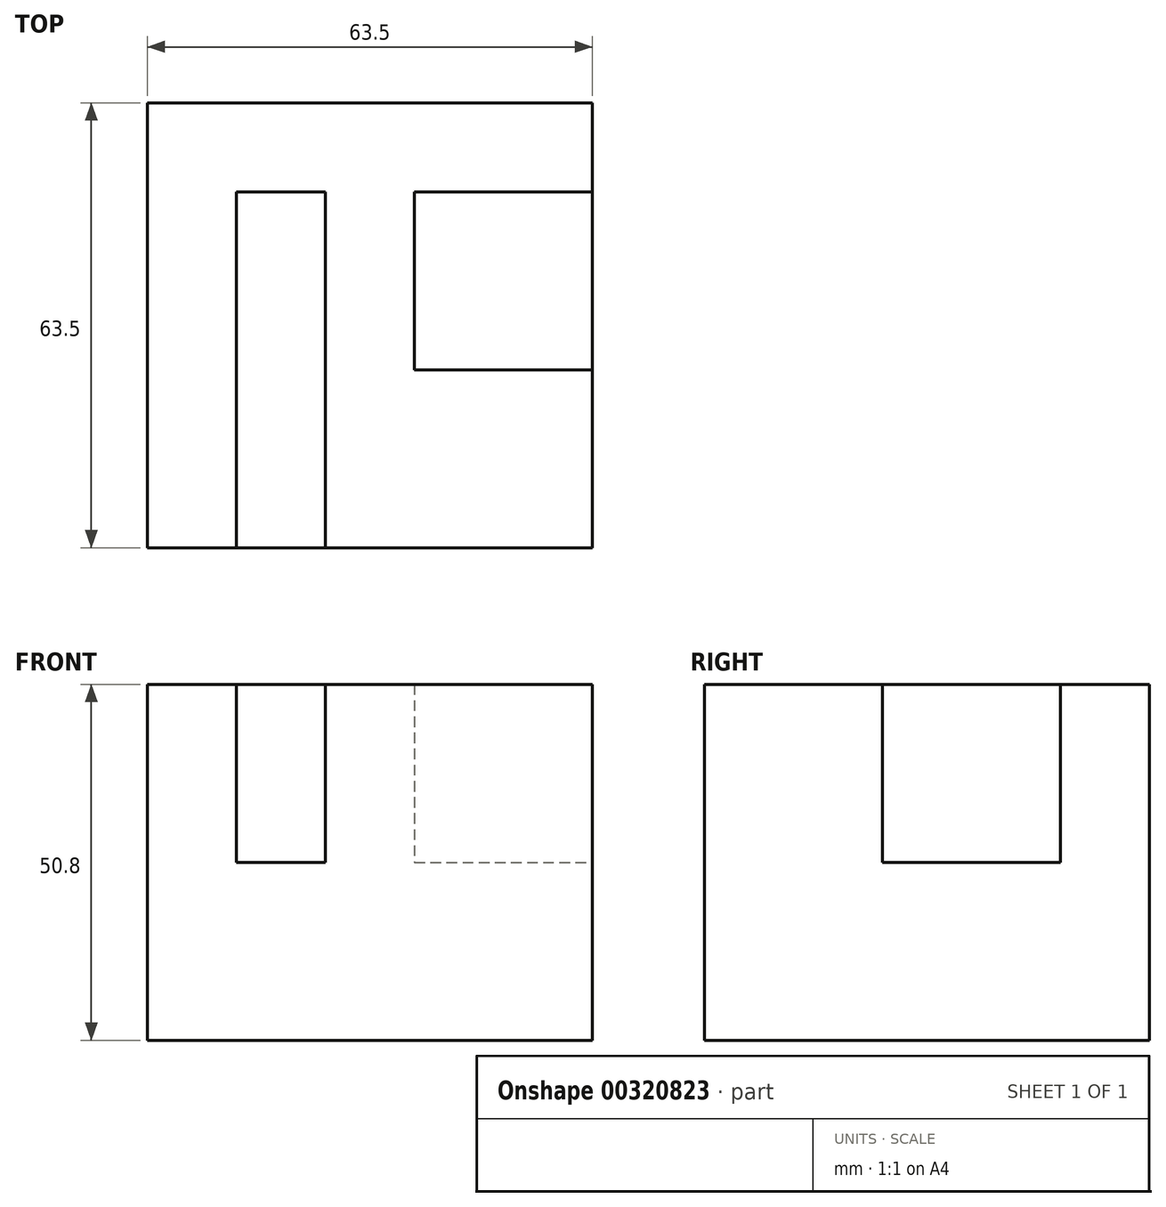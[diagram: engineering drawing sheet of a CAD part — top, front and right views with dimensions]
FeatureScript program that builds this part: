
annotation { "Feature Type Name" : "Feature", "Feature Type Description" : "" }
export const myFeature = defineFeature(function(context is Context, id is Id, definition is map)
    precondition{}
    {
        {
            var Q0;
            Q0=qCreatedBy(makeId("Front.planeOp"),FACE);
            var sketch = newSketch(context, id + "F0", { "sketchPlane" : qUnion([Q0])});
            skLineSegment(sketch, "E0", {"start": v(-39.9, -57.03) * mm, "end": v(23.6, -57.03) * mm});
            skLineSegment(sketch, "E1", {"start": v(23.6, -57.03) * mm, "end": v(23.6, -6.23) * mm});
            skLineSegment(sketch, "E2", {"start": v(23.6, -6.23) * mm, "end": v(-39.9, -6.23) * mm});
            skLineSegment(sketch, "E3", {"start": v(-39.9, -6.23) * mm, "end": v(-39.9, -57.03) * mm});
            skSolve(sketch);
        }
        {
            var Q0;
            Q0=makeQuery(id+"F0.imprint","IMPRINT",FACE,{"disambiguationData":[TD([[makeQuery(id+"F0.imprint","IMPRINT",EDGE,{"derivedFrom":sQuery(id+"F0.wireOp",EDGE,"E0")}),1.0]])]});
            extrude(context, id + "F1", {"entities" : qUnion([Q0]), "oppositeDirection" : true, "depth" : 63.5 * mm});
        }
        {
            var Q0;
            Q0=makeQuery(id+"F1.opExtrude","CAP_FACE",FACE,{"disambiguationData":[OSD([sQuery(id+"F0.wireOp",EDGE,"E0"),sQuery(id+"F0.wireOp",EDGE,"E1"),sQuery(id+"F0.wireOp",EDGE,"E2"),sQuery(id+"F0.wireOp",EDGE,"E3")])],"isStart":true});
            var sketch = newSketch(context, id + "F2", { "sketchPlane" : qUnion([Q0])});
            skLineSegment(sketch, "E4", {"start": v(-39.9, -6.23) * mm, "end": v(-27.2, -6.23) * mm});
            skLineSegment(sketch, "E5", {"start": v(-27.2, -6.23) * mm, "end": v(-14.5, -6.23) * mm});
            skLineSegment(sketch, "E6", {"start": v(-14.5, -6.23) * mm, "end": v(-14.5, -31.63) * mm});
            skLineSegment(sketch, "E7", {"start": v(-14.5, -31.63) * mm, "end": v(-27.2, -31.63) * mm});
            skLineSegment(sketch, "E8", {"start": v(-27.2, -31.63) * mm, "end": v(-27.2, -6.23) * mm});
            skLineSegment(sketch, "E9", {"start": v(-14.5, -6.23) * mm, "end": v(-27.2, -6.23) * mm});
            skSolve(sketch);
        }
        {
            var Q0;
            Q0=makeQuery(id+"F2.imprint","IMPRINT",FACE,{"disambiguationData":[TD([[makeQuery(id+"F2.imprint","IMPRINT",EDGE,{"derivedFrom":sQuery(id+"F2.wireOp",EDGE,"E6")}),-1.0]])]});
            extrude(context, id + "F3", {"entities" : qUnion([Q0]), "operationType" : NewBodyOperationType.REMOVE, "oppositeDirection" : true, "depth" : 50.8 * mm});
        }
        {
            var Q0;
            Q0=makeQuery(id+"F1.opExtrude","SWEPT_FACE",FACE,{"disambiguationData":[OSD([sQuery(id+"F0.wireOp",EDGE,"E1")])]});
            var sketch = newSketch(context, id + "F4", { "sketchPlane" : qUnion([Q0])});
            skLineSegment(sketch, "E10", {"start": v(0, -6.23) * mm, "end": v(25.4, -6.23) * mm});
            skLineSegment(sketch, "E11", {"start": v(25.4, -6.23) * mm, "end": v(25.4, -31.63) * mm});
            skLineSegment(sketch, "E12", {"start": v(25.4, -31.63) * mm, "end": v(50.8, -31.63) * mm});
            skLineSegment(sketch, "E13", {"start": v(50.8, -31.63) * mm, "end": v(50.8, -6.23) * mm});
            skLineSegment(sketch, "E14", {"start": v(50.8, -6.23) * mm, "end": v(25.4, -6.23) * mm});
            skSolve(sketch);
        }
        {
            var Q0;
            Q0=makeQuery(id+"F4.imprint","IMPRINT",FACE,{"disambiguationData":[TD([[makeQuery(id+"F4.imprint","IMPRINT",EDGE,{"derivedFrom":sQuery(id+"F4.wireOp",EDGE,"E11")}),1.0]])]});
            extrude(context, id + "F5", {"entities" : qUnion([Q0]), "operationType" : NewBodyOperationType.REMOVE, "oppositeDirection" : true, "depth" : 25.4 * mm});
        }
    });
